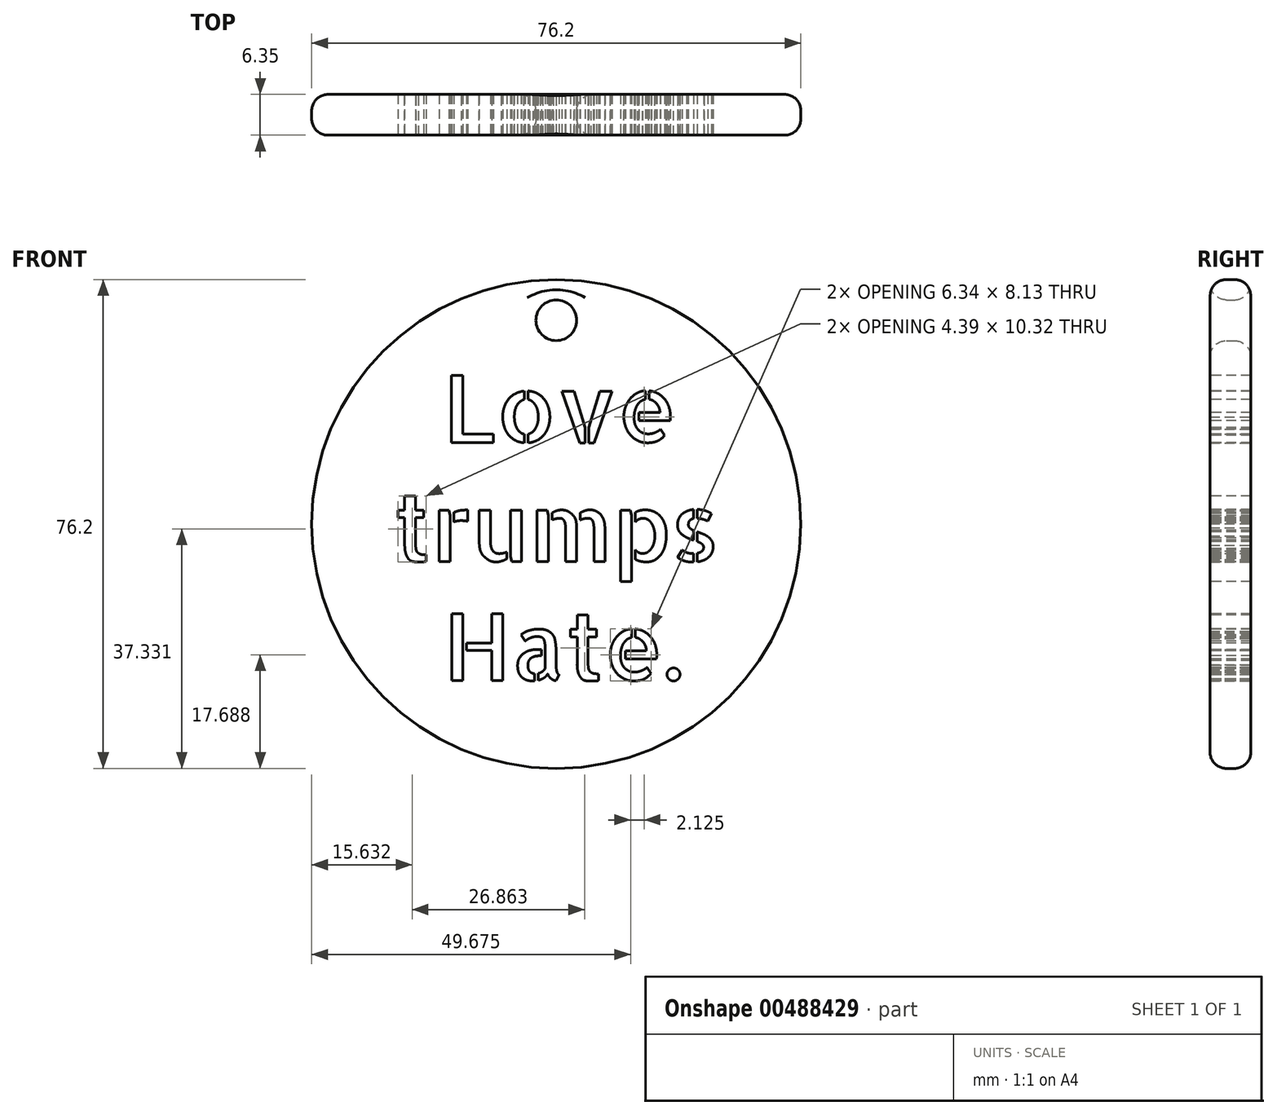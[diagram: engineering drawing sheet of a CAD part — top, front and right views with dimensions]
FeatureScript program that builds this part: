
annotation { "Feature Type Name" : "Feature", "Feature Type Description" : "" }
export const myFeature = defineFeature(function(context is Context, id is Id, definition is map)
    precondition{}
    {
        {
            var Q0;
            Q0=qCreatedBy(makeId("Front.planeOp"),FACE);
            var sketch = newSketch(context, id + "F0", { "sketchPlane" : qUnion([Q0])});
            skCircle(sketch, "E0", {"center": v(0, 0) * mm, "radius": 38.1 * mm});
            skCircle(sketch, "E1", {"center": v(0, 31.75) * mm, "radius": 3.18 * mm});
            skSolve(sketch);
        }
        {
            var Q0;
            Q0 = qSketchRegion(id + "F0", true);
            extrude(context, id + "F1", {"entities" : qUnion([Q0]), "depth" : 6.35 * mm});
        }
        {
            var Q0;
            Q0=makeQuery(id+"F1.opExtrude","CAP_EDGE",EDGE,{"disambiguationData":[OSD([sQuery(id+"F0.wireOp",EDGE,"E0")])],"isStart":false});
            var Q1;
            Q1=makeQuery(id+"F1.opExtrude","CAP_EDGE",EDGE,{"disambiguationData":[OSD([sQuery(id+"F0.wireOp",EDGE,"E1")])],"isStart":false});
            var Q2;
            Q2=makeQuery(id+"F1.opExtrude","CAP_EDGE",EDGE,{"disambiguationData":[OSD([sQuery(id+"F0.wireOp",EDGE,"E0")])],"isStart":true});
            var Q3;
            Q3=makeQuery(id+"F1.opExtrude","CAP_EDGE",EDGE,{"disambiguationData":[OSD([sQuery(id+"F0.wireOp",EDGE,"E1")])],"isStart":true});
            fillet(context, id + "F2", {"entities" : qUnion([Q0, Q1, Q2, Q3]), "radius" : 2.54 * mm, "tangentPropagation" : true, "allowEdgeOverflow" : false});
        }
        {
            var Q0;
            Q0=makeQuery(id+"F1.opExtrude","CAP_FACE",FACE,{"disambiguationData":[OSD([sQuery(id+"F0.wireOp",EDGE,"E0"),sQuery(id+"F0.wireOp",EDGE,"E1")])],"isStart":false});
            var sketch = newSketch(context, id + "F3", { "sketchPlane" : qUnion([Q0])});
            skText(sketch, "E2", { "text": "  Love\ntrumps\n  Hate.", "fontName": "AllertaStencil-Regular.ttf"});
            const initialGuessF3  = {"E2": [-0.0254, 0.0127, 1, 0, 0.01044]};
            skSetInitialGuess(sketch, initialGuessF3);
            skSolve(sketch);
        }
        {
            var Q0;
            Q0 = qSketchRegion(id + "F3", true);
            extrude(context, id + "F4", {"entities" : qUnion([Q0]), "operationType" : NewBodyOperationType.REMOVE, "endBound" : BoundingType.THROUGH_ALL, "oppositeDirection" : true, "depth" : 25.4 * mm});
        }
    });
